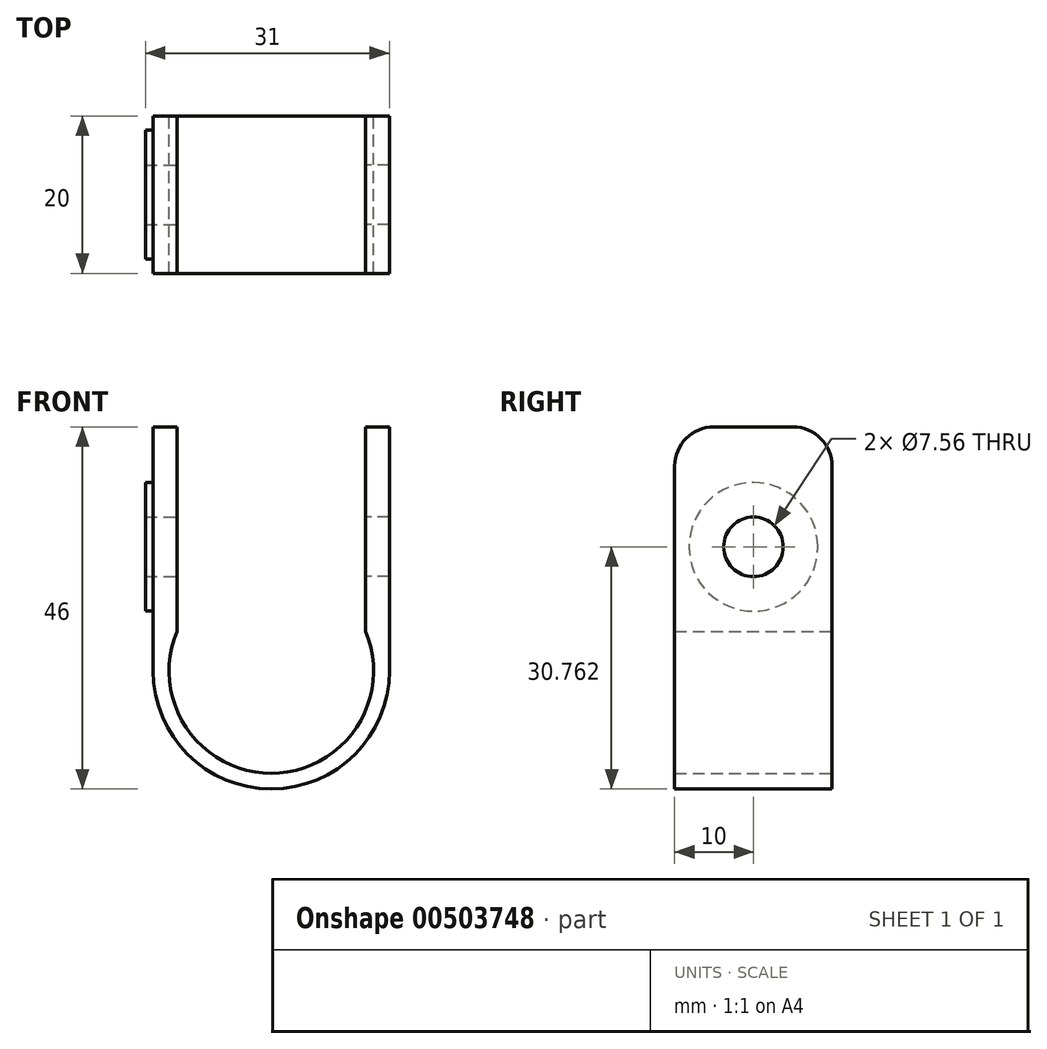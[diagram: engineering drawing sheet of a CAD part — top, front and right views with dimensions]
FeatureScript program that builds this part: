
annotation { "Feature Type Name" : "Feature", "Feature Type Description" : "" }
export const myFeature = defineFeature(function(context is Context, id is Id, definition is map)
    precondition{}
    {
        {
            var Q0;
            Q0=qCreatedBy(makeId("Front.planeOp"),FACE);
            var sketch = newSketch(context, id + "F0", { "sketchPlane" : qUnion([Q0])});
            skArc(sketch, "E0", {"start": v(-12, 5) * mm, "mid": v(0, -13) * mm, "end": v(12, 5) * mm});
            skArc(sketch, "E1", {"start": v(-15, 0) * mm, "mid": v(0, -15) * mm, "end": v(15, 0) * mm});
            skLineSegment(sketch, "E2", {"start": v(-15, 0) * mm, "end": v(-15, 31) * mm});
            skLineSegment(sketch, "E3", {"start": v(15, 0) * mm, "end": v(15, 31) * mm});
            skLineSegment(sketch, "E4", {"start": v(15, 31) * mm, "end": v(12, 31) * mm});
            skLineSegment(sketch, "E5", {"start": v(-12, 5) * mm, "end": v(-12, 31) * mm});
            skLineSegment(sketch, "E6", {"start": v(12, 5) * mm, "end": v(12, 31) * mm});
            skLineSegment(sketch, "E7.trimOffspring", {"start": v(-12, 31) * mm, "end": v(-15, 31) * mm});
            skSolve(sketch);
        }
        {
            var Q0;
            Q0 = qSketchRegion(id + "F0", true);
            extrude(context, id + "F1", {"entities" : qUnion([Q0]), "depth" : 20 * mm});
        }
        {
            var Q0;
            Q0=makeQuery(id+"F1.opExtrude","SWEPT_FACE",FACE,{"disambiguationData":[OSD([sQuery(id+"F0.wireOp",EDGE,"E2")])]});
            var sketch = newSketch(context, id + "F2", { "sketchPlane" : qUnion([Q0])});
            skCircle(sketch, "E8", {"center": v(10, 15.76) * mm, "radius": 8.18 * mm});
            skPoint(sketch, "E8.centerSnap0", {"position": v(10, 31) * mm});
            skCircle(sketch, "E9", {"center": v(10, 15.76) * mm, "radius": 3.78 * mm});
            skSolve(sketch);
        }
        {
            var Q0;
            Q0 = qSketchRegion(id + "F2", true);
            extrude(context, id + "F3", {"entities" : qUnion([Q0]), "operationType" : NewBodyOperationType.ADD, "offsetDistance" : 25 * mm, "depth" : 1 * mm});
        }
        {
            var Q0;
            Q0=makeQuery(id+"F3.boolean.opBoolean","SPLIT",FACE,{"disambiguationData":[TD([makeQuery(id+"F3.opExtrude","SWEPT_FACE",FACE,{"disambiguationData":[OSD([sQuery(id+"F2.wireOp",EDGE,"E9")])]})])],"derivedFrom":makeQuery(id+"F1.opExtrude","SWEPT_FACE",FACE,{"disambiguationData":[OSD([sQuery(id+"F0.wireOp",EDGE,"E2")])]})});
            extrude(context, id + "F4", {"entities" : qUnion([Q0]), "operationType" : NewBodyOperationType.REMOVE, "oppositeDirection" : true, "depth" : 47.6 * mm});
        }
        {
            var Q0;
            Q0=makeQuery(id+"F1.opExtrude","CAP_EDGE",EDGE,{"disambiguationData":[OSD([sQuery(id+"F0.wireOp",EDGE,"E7.trimOffspring")])],"isStart":false});
            var Q1;
            Q1=makeQuery(id+"F1.opExtrude","CAP_EDGE",EDGE,{"disambiguationData":[OSD([sQuery(id+"F0.wireOp",EDGE,"E7.trimOffspring")])],"isStart":true});
            var Q2;
            Q2=makeQuery(id+"F1.opExtrude","CAP_EDGE",EDGE,{"disambiguationData":[OSD([sQuery(id+"F0.wireOp",EDGE,"E4")])],"isStart":false});
            var Q3;
            Q3=makeQuery(id+"F1.opExtrude","CAP_EDGE",EDGE,{"disambiguationData":[OSD([sQuery(id+"F0.wireOp",EDGE,"E4")])],"isStart":true});
            fillet(context, id + "F5", {"entities" : qUnion([Q0, Q1, Q2, Q3]), "radius" : 5 * mm, "tangentPropagation" : true, "allowEdgeOverflow" : false});
        }
    });
